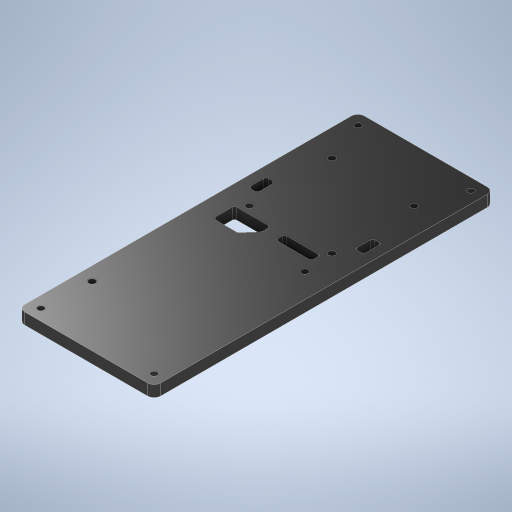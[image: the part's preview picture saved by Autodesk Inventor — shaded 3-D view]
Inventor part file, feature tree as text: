
AUTODESK INVENTOR PART (.ipt)
format: ipt  version: 2023 (Build 270158000, 158)  size: 353,280 bytes
history: native  units: in
note: dims shown in document units (in); Inventor stores cm internally (conversion verified against a paired STEP export)
features: extrude x6, fillet x3, sketch x1
ambient origin geometry x8: Origin, YZ Plane, XZ Plane, XY Plane, X Axis, Y Axis, Z Axis, Center Point
bodies: Solid1 (feature_tree)
feature tree (10):
  sketch  "Sketch1"  dims[d10=2.3622in d11=5.9055in d12=0.1969in d13=0.1969in d14=0.1969in d15=0.1969in d16=0.1969in d17=0.1969in d18=0.1969in d19=0.1969in d20=0.1102in d21=0.1102in d22=0.1102in d23=0.1102in d24=0.1969in d25=0.0in d26=0.1102in d27=0.1102in d28=0.7874in d29=0.8465in d30=1.6929in d31=0.8465in d32=1.4331in d33=1.4331in d34=0.1181in d35=0.1181in d36=0.1181in d37=0.1181in d38=0.426in d39=3.0472in d40=0.2362in d41=1.0472in d42=0.1181in d43=0.1181in d44=0.3937in d45=0.0in d46=0.3937in d47=0.0in d48=0.3937in d49=0.1575in d50=0.315in d51=0.1575in d52=0.315in d53=0.2362in d54=0.3937in d55=0.1575in d56=0.1969in d57=0.6299in d58=0.1575in d59=0.3937in d60=0.0in d61=0.3937in d62=0.0in d63=0.3937in d64=0.0in d65=0.0394in]
  extrude  "Extrusion1"  Depth=5.9055in
  fillet  "Fillet1"  Radius=0.1969in
  fillet  "Fillet2"  Radius=0.1969in
  extrude  "Extrusion2"  Depth=0.1969in
  extrude  "Extrusion3"  Depth=0.1969in
  extrude  "Extrusion4"  Depth=0.1969in
  extrude  "Extrusion5"  Depth=0.1969in
  extrude  "Extrusion6"  Depth=0.1969in
  fillet  "Fillet3"  Radius=0.1969in
